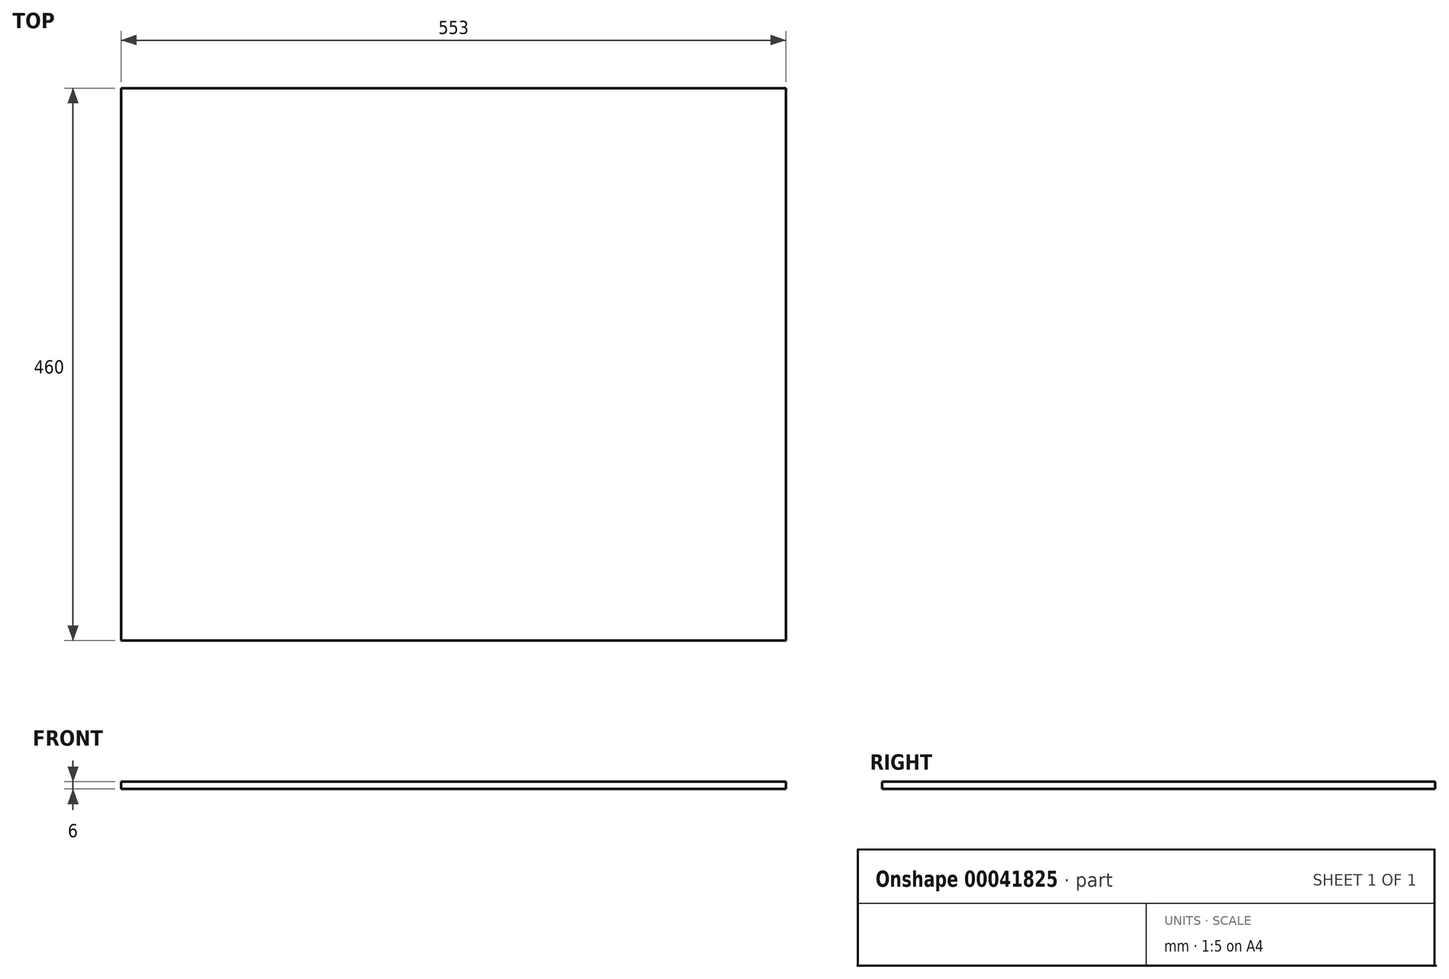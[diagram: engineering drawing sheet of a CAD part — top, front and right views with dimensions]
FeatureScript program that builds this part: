
annotation { "Feature Type Name" : "Feature", "Feature Type Description" : "" }
export const myFeature = defineFeature(function(context is Context, id is Id, definition is map)
    precondition{}
    {
        {
            var Q0;
            Q0=qCreatedBy(makeId("Front.planeOp"),FACE);
            var sketch = newSketch(context, id + "F0", { "sketchPlane" : qUnion([Q0])});
            skLineSegment(sketch, "E0.bottom", {"start": v(0, 0) * mm, "end": v(553, 0) * mm});
            skLineSegment(sketch, "E0.top", {"start": v(0, 6) * mm, "end": v(553, 6) * mm});
            skLineSegment(sketch, "E0.left", {"start": v(0, 0) * mm, "end": v(0, 6) * mm});
            skLineSegment(sketch, "E0.right", {"start": v(553, 0) * mm, "end": v(553, 6) * mm});
            skSolve(sketch);
        }
        {
            var Q0;
            Q0=makeQuery(id+"F0.imprint","IMPRINT",FACE,{"disambiguationData":[TD([[makeQuery(id+"F0.imprint","IMPRINT",EDGE,{"derivedFrom":sQuery(id+"F0.wireOp",EDGE,"E0.bottom")}),1.0]])]});
            extrude(context, id + "F1", {"entities" : qUnion([Q0]), "endBound" : BoundingType.SYMMETRIC, "depth" : 460 * mm});
        }
    });
